annotation { "Feature Type Name" : "Feature", "Feature Type Description" : "" }
export const myFeature = defineFeature(function(context is Context, id is Id, definition is map)
    precondition{}
    {
        {
            var Q0;
            Q0=qCreatedBy(makeId("Front.planeOp"),FACE);
            var sketch = newSketch(context, id + "F0", { "sketchPlane" : qUnion([Q0])});
            skFitSpline(sketch, "E0", {"points": [v(-88.56, -40.8) * mm, v(-85.82, -38.7) * mm, v(-82.34, -35.61) * mm, v(-78.68, -33.27) * mm, v(-74.23, -31.45) * mm, v(-69.9, -30.82) * mm, v(-66.52, -29.56) * mm, v(-64.93, -24.6) * mm, v(-64.3, -20.26) * mm, v(-62.13, -8.79) * mm, v(-58.76, 0) * mm, v(-31.82, 31.51) * mm, v(-31.88, 34.48) * mm, v(-35.01, 41.67) * mm, v(-42.44, 49.9) * mm, v(-43.98, 53.43) * mm, v(-37.93, 54.29) * mm, v(-23.48, 51.55) * mm, v(-9.04, 46.13) * mm, v(-4.48, 45.33) * mm, v(2.37, 46.7) * mm, v(10.48, 48.41) * mm, v(23.27, 50.8) * mm, v(35.02, 51.66) * mm, v(47.7, 51.5) * mm, v(59.74, 48.41) * mm, v(70.47, 44.87) * mm, v(77.72, 39.96) * mm, v(83.03, 33.28) * mm, v(83.03, 31.11) * mm, v(82, 29.8) * mm, v(71.56, 34.37) * mm, v(80.98, 28.83) * mm, v(82, 27.75) * mm, v(79.83, 26.1) * mm, v(75.1, 24.95) * mm, v(71.44, 22.44) * mm, v(64.6, 19.01) * mm, v(56.14, 14.67) * mm, v(39.53, 6.4) * mm, v(19.84, 2) * mm, v(7.05, -1.08) * mm, v(2.52, -1.7) * mm, v(-5.39, -2.26) * mm, v(-12.25, -2.82) * mm, v(-20.8, -2.9) * mm, v(-23.88, -4.04) * mm, v(-27.5, -6.98) * mm, v(-31.99, -10.05) * mm, v(-39.33, -14.65) * mm, v(-42.2, -16.23) * mm, v(-47.37, -22.84) * mm, v(-55, -32.2) * mm, v(-56.85, -34.87) * mm, v(-51.69, -47.47) * mm, v(-50.46, -48.14) * mm, v(-50.08, -49.7) * mm, v(-49.07, -53.34) * mm, v(-48.64, -56.54) * mm, v(-48.52, -60.66) * mm, v(-51.5, -67.45) * mm, v(-57.48, -65) * mm, v(-60.74, -57.68) * mm, v(-65.62, -51.43) * mm, v(-68.88, -46) * mm, v(-75.67, -45.19) * mm, v(-83.82, -40.84) * mm, v(-88.56, -40.8) * mm]});
            skFitSpline(sketch, "E1", {"points": [v(49.15, 16.18) * mm, v(40.93, 11.84) * mm, v(36.93, 0) * mm, v(30.08, -12.25) * mm, v(19.23, -16.7) * mm, v(10.22, -16.7) * mm, v(15.01, -10.2) * mm, v(20.15, 0) * mm, v(22.09, 7.39) * mm, v(27.45, 10.81) * mm, v(49.15, 16.18) * mm]});
            skFitSpline(sketch, "E2", {"points": [v(50.43, 11.45) * mm, v(50.52, 6.47) * mm, v(50.29, 0) * mm, v(45.83, -9.97) * mm, v(38.76, -15.56) * mm, v(38.98, -9.5) * mm, v(39.67, -2.43) * mm, v(38.76, 3.85) * mm, v(39.53, 6.4) * mm, v(50.43, 11.45) * mm]});
            skSolve(sketch);
        }
        {
            var Q0;
            {var subQ0=sQuery(id+"F0.wireOp",EDGE,"E2");var subQ1=sQuery(id+"F0.wireOp",EDGE,"E0");var subQ2=makeQuery(id+"F0.imprint","INTERSECT",VERTEX,{"disambiguationData":[OD(0.0)],"derivedFrom":[subQ1,subQ0]});Q0=makeQuery(id+"F0.imprint","IMPRINT",FACE,{"disambiguationData":[TD([[makeQuery(id+"F0.imprint","IMPRINT",EDGE,{"disambiguationData":[TD([[subQ2,-1.0]])],"derivedFrom":subQ1}),-1.0]])]});}
            var Q1;
            {var subQ0=sQuery(id+"F0.wireOp",EDGE,"E1");var subQ1=sQuery(id+"F0.wireOp",EDGE,"E0");var subQ2=makeQuery(id+"F0.imprint","INTERSECT",VERTEX,{"disambiguationData":[OD(0.0)],"derivedFrom":[subQ1,subQ0]});Q1=makeQuery(id+"F0.imprint","IMPRINT",FACE,{"disambiguationData":[TD([[makeQuery(id+"F0.imprint","IMPRINT",EDGE,{"disambiguationData":[TD([[subQ2,-1.0]])],"derivedFrom":subQ1}),-1.0]])]});}
            var Q2;
            {var subQ0=sQuery(id+"F0.wireOp",EDGE,"E1");var subQ1=sQuery(id+"F0.wireOp",EDGE,"E0");var subQ2=makeQuery(id+"F0.imprint","INTERSECT",VERTEX,{"disambiguationData":[OD(0.0)],"derivedFrom":[subQ1,subQ0]});Q2=makeQuery(id+"F0.imprint","IMPRINT",FACE,{"disambiguationData":[TD([[makeQuery(id+"F0.imprint","IMPRINT",EDGE,{"disambiguationData":[TD([[subQ2,-1.0]])],"derivedFrom":subQ1}),1.0]])]});}
            var Q3;
            {var subQ0=sQuery(id+"F0.wireOp",EDGE,"E2");var subQ1=sQuery(id+"F0.wireOp",EDGE,"E0");var subQ2=makeQuery(id+"F0.imprint","INTERSECT",VERTEX,{"disambiguationData":[OD(0.0)],"derivedFrom":[subQ1,subQ0]});Q3=makeQuery(id+"F0.imprint","IMPRINT",FACE,{"disambiguationData":[TD([[makeQuery(id+"F0.imprint","IMPRINT",EDGE,{"disambiguationData":[TD([[subQ2,1.0]])],"derivedFrom":subQ1}),1.0]])]});}
            extrude(context, id + "F1", {"entities" : qUnion([Q0, Q1, Q2, Q3]), "depth" : 25.4 * mm});
        }
        {
            var Q0;
            Q0=makeQuery(id+"F1.opExtrude","CAP_FACE",FACE,{"disambiguationData":[OSD([sQuery(id+"F0.wireOp",EDGE,"E0"),sQuery(id+"F0.wireOp",EDGE,"E1"),sQuery(id+"F0.wireOp",EDGE,"E2")])],"isStart":false});
            var sketch = newSketch(context, id + "F2", { "sketchPlane" : qUnion([Q0])});
            skText(sketch, "E3", { "text": "Lego Minds\n", "fontName": "OpenSans-Regular.ttf"});
            skText(sketch, "E4", { "text": "29620\n", "fontName": "OpenSans-Regular.ttf"});
            const initialGuessF2  = {"E3": [-0.04348, 0.0064, 1, 0, 0.01113], "E4": [-0.02198, 0.02298, 1, 0, 0.01382]};
            skSetInitialGuess(sketch, initialGuessF2);
            skSolve(sketch);
        }
        {
            var Q0;
            Q0 = qSketchRegion(id + "F2", true);
            extrude(context, id + "F3", {"entities" : qUnion([Q0]), "operationType" : NewBodyOperationType.ADD, "depth" : 1.27 * mm});
        }
        {
            var Q0;
            Q0=makeQuery(id+"F1.opExtrude","CAP_FACE",FACE,{"disambiguationData":[OSD([sQuery(id+"F0.wireOp",EDGE,"E0"),sQuery(id+"F0.wireOp",EDGE,"E1"),sQuery(id+"F0.wireOp",EDGE,"E2")])],"isStart":true});
            var sketch = newSketch(context, id + "F4", { "sketchPlane" : qUnion([Q0])});
            skText(sketch, "E5", { "text": "Save", "fontName": "OpenSans-Regular.ttf"});
            skText(sketch, "E6", { "text": "Vaquitas", "fontName": "OpenSans-Regular.ttf"});
            const initialGuessF4  = {"E5": [-0.04266, 0.02666, 1, 0, 0.0096], "E6": [-0.03498, 0.00477, 1, 0, 0.0119]};
            skSetInitialGuess(sketch, initialGuessF4);
            skSolve(sketch);
        }
        {
            var Q0;
            Q0 = qSketchRegion(id + "F4", true);
            extrude(context, id + "F5", {"entities" : qUnion([Q0]), "operationType" : NewBodyOperationType.ADD, "depth" : 1.27 * mm});
        }
        {
            var Q0;
            Q0=qCreatedBy(makeId("Front.planeOp"),FACE);
            var sketch = newSketch(context, id + "F6", { "sketchPlane" : qUnion([Q0])});
            skLineSegment(sketch, "E7.bottom", {"start": v(5.77, 0) * mm, "end": v(-3.44, 0) * mm});
            skLineSegment(sketch, "E7.top", {"start": v(5.77, -47.45) * mm, "end": v(-3.44, -47.45) * mm});
            skLineSegment(sketch, "E7.left", {"start": v(5.77, 0) * mm, "end": v(5.77, -47.45) * mm});
            skLineSegment(sketch, "E7.right", {"start": v(-3.44, 0) * mm, "end": v(-3.44, -47.45) * mm});
            skSolve(sketch);
        }
        {
            var Q0;
            Q0=makeQuery(id+"F6.imprint","IMPRINT",FACE,{"disambiguationData":[TD([[makeQuery(id+"F6.imprint","IMPRINT",EDGE,{"derivedFrom":sQuery(id+"F6.wireOp",EDGE,"E7.bottom")}),1.0]])]});
            extrude(context, id + "F7", {"entities" : qUnion([Q0]), "operationType" : NewBodyOperationType.ADD, "depth" : 25.4 * mm});
        }
        {
            var Q0;
            Q0=makeQuery(id+"F7.opExtrude","SWEPT_FACE",FACE,{"disambiguationData":[OSD([sQuery(id+"F6.wireOp",EDGE,"E7.top")])]});
            var sketch = newSketch(context, id + "F8", { "sketchPlane" : qUnion([Q0])});
            skEllipse(sketch, "E8", {"center": v(0, 13.3) * mm, "majorRadius": 19.71 * mm, "minorRadius": 12.33 * mm, "majorAxis": v(0.65, -0.76)});
            skSolve(sketch);
        }
        {
            var Q0;
            Q0 = qSketchRegion(id + "F8", true);
            extrude(context, id + "F9", {"entities" : qUnion([Q0]), "operationType" : NewBodyOperationType.ADD, "depth" : 23.62 * mm});
        }
    });